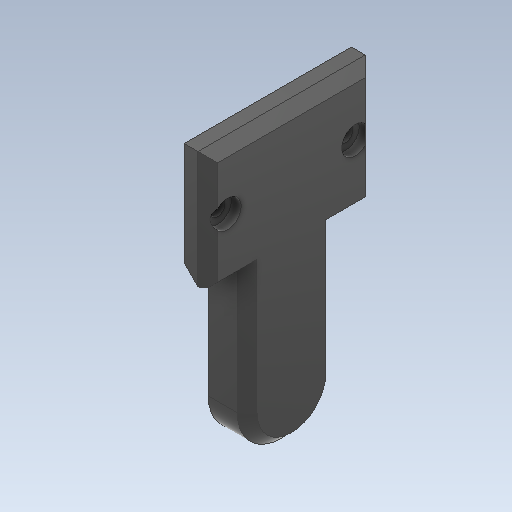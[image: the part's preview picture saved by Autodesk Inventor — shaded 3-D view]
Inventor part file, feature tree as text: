
AUTODESK INVENTOR PART (.ipt)
format: ipt  version: 2020 (Build 240168000, 168)  size: 206,848 bytes
history: native  units: in
note: dims shown in document units (in); Inventor stores cm internally (conversion verified against a paired STEP export)
features: sketch x19, other x4, plane x2
ambient origin geometry x8: Origin, YZ Plane, XZ Plane, XY Plane, X Axis, Y Axis, Z Axis, Center Point
bodies: Solid1 (feature_tree), Solid2 (feature_tree)
feature tree (25):
  other  "FemurSupportBot.ipt"
  other  "Solid1::FemurSupportBot.ipt"
  other  "Solid2::FemurSupportBot.ipt"
  other  "TaggingFeature1"
  sketch  "Sketch1"  dims[d0=0.3937in]
  sketch  "Sketch2"
  sketch  "Sketch3"
  sketch  "Sketch4"
  sketch  "Sketch5"
  sketch  "Sketch6"
  sketch  "Sketch8"
  sketch  "Sketch10"
  sketch  "Sketch11"
  sketch  "Sketch12"
  sketch  "Sketch13"
  sketch  "Sketch14"
  sketch  "Sketch15"
  sketch  "Sketch17"
  sketch  "Sketch19"
  sketch  "Sketch20"
  sketch  "Sketch21"
  sketch  "Sketch22"
  sketch  "Sketch23"
  plane  "Work Plane1"
  plane  "Work Plane2"
